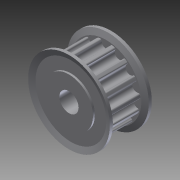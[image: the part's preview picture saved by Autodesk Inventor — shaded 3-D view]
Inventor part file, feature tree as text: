
AUTODESK INVENTOR PART (.ipt)
format: ipt  version: 2012 (Build 160160000, 160)  size: 296,960 bytes
history: native  units: in
note: dims shown in document units (in); Inventor stores cm internally (conversion verified against a paired STEP export)
features: extrude x2, sketch x2, imported_body x1
ambient origin geometry x8: Origin, YZ Plane, XZ Plane, XY Plane, X Axis, Y Axis, Z Axis, Center Point
feature tree (5):
  extrude  "Extrusion1"  Depth=0.0394in
  extrude  "Extrusion2"  Depth=0.248in TaperAngle=0.0deg
  imported_body  "Base1"
  sketch  "Sketch1"  dims[d0=0.25in d1=0.0394in]
  sketch  "Sketch2"  dims[d8=0.3937in d9=0.0in d10=0.248in d11=0.0in]
